# Revit family: EMEA Cabinet DN150_Metric
name_source: partatom
category: Pipe Accessories
revit_build: Autodesk Revit 2018 (Build: 20170630_0700(x64)
units: mm (PartAtom-declared; Revit-internal decimal feet)

## family parameters
Always vertical = Yes
Cut with Voids When Loaded = No
OmniClass Number = 23.65.55.00
OmniClass Title = Distribution of Supplied Liquids/Gases
Part Type = Normal
Round Connector Dimension = Use Diameter
Shared = No
Work Plane-Based = No

## types (1)
- Tyco_Cabinet EMEA_DN150_Red-E
    Description = DN150 Red-E Cabinet EMEA
    Drain Pipe OD = 50 mm  [stored 0.164042 ft]
    Manufacturer = Tyco Fire Protection Products
    Manufacturer URL = https://www.tyco-fire.com
    Pipe Inlet OD = 150 mm  [stored 0.492126 ft]
    Pipe Outlet OD = 150 mm  [stored 0.492126 ft]
    Technical Data Sheet No = TFP1401 / TFP1301

note: [stored X ft] marks values corroborated as IEEE doubles in the binary element streams (Revit-internal decimal feet)

## geometry (parser evidence)
native form markers: Sweep x2
no freeform markers — native parametric forms only
